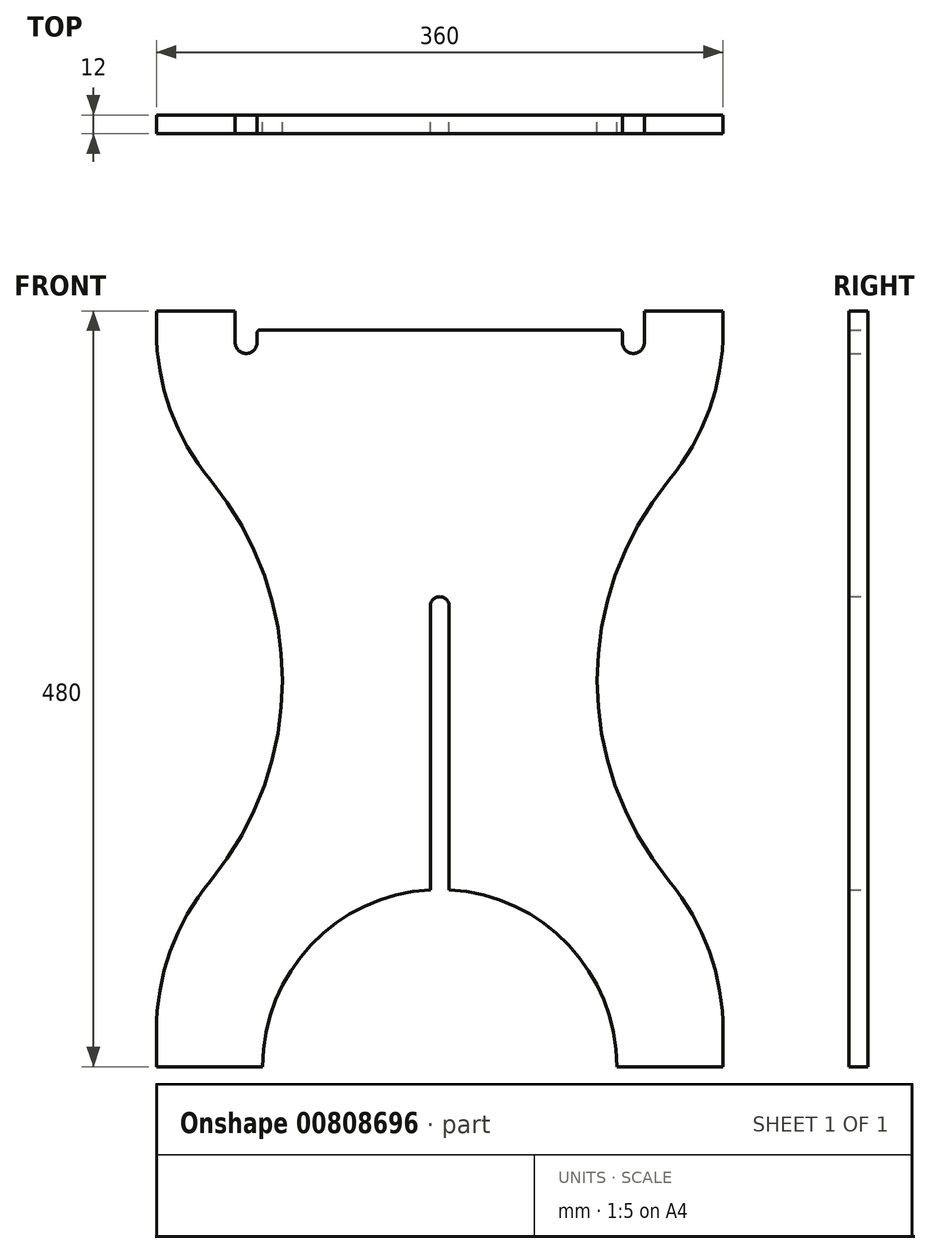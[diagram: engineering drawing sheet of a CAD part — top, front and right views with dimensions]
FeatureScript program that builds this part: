
annotation { "Feature Type Name" : "Feature", "Feature Type Description" : "" }
export const myFeature = defineFeature(function(context is Context, id is Id, definition is map)
    precondition{}
    {
        {
            var Q0;
            Q0=qCreatedBy(makeId("Front.planeOp"),FACE);
            var sketch = newSketch(context, id + "F0", { "sketchPlane" : qUnion([Q0])});
            skLineSegment(sketch, "E0.bottom", {"start": v(-180, -240) * mm, "end": v(-112.5, -240) * mm});
            skLineSegment(sketch, "E0.top", {"start": v(-180, 240) * mm, "end": v(-130, 240) * mm});
            skLineSegment(sketch, "E0.left", {"start": v(-180, -240) * mm, "end": v(-180, -217.42) * mm});
            skLineSegment(sketch, "E0.right", {"start": v(180, -240) * mm, "end": v(180, -217.42) * mm});
            skPoint(sketch, "E0.middle", {"position": v(0, 0) * mm});
            skLineSegment(sketch, "E1.0", {"start": v(-130, 228) * mm, "end": v(-130, 240) * mm});
            skLineSegment(sketch, "E2.0", {"start": v(130, 228) * mm, "end": v(130, 240) * mm});
            skLineSegment(sketch, "E3.trimOffspring", {"start": v(130, 240) * mm, "end": v(180, 240) * mm});
            skArc(sketch, "E4", {"start": v(112.5, -240) * mm, "mid": v(81.64, -162.6) * mm, "end": v(6, -127.66) * mm});
            skLineSegment(sketch, "E5.trimOffspring", {"start": v(112.5, -240) * mm, "end": v(180, -240) * mm});
            skArc(sketch, "E6", {"start": v(145.71, 132.55) * mm, "mid": v(100, 5.29) * mm, "end": v(145.71, -121.97) * mm});
            skArc(sketch, "E7", {"start": v(-145.71, -121.97) * mm, "mid": v(-100, 5.29) * mm, "end": v(-145.71, 132.55) * mm});
            skLineSegment(sketch, "E8.trimOffspring", {"start": v(-180, 228) * mm, "end": v(-180, 240) * mm});
            skLineSegment(sketch, "E9.trimOffspring", {"start": v(180, 228) * mm, "end": v(180, 240) * mm});
            skPoint(sketch, "E10.visualSharp", {"position": v(-180, 165.29) * mm});
            skArc(sketch, "E10.filletArc", {"start": v(-180, 228) * mm, "mid": v(-171.17, 177.3) * mm, "end": v(-145.71, 132.55) * mm});
            skPoint(sketch, "E11.visualSharp", {"position": v(-180, -154.71) * mm});
            skArc(sketch, "E11.filletArc", {"start": v(-145.71, -121.97) * mm, "mid": v(-171.17, -166.71) * mm, "end": v(-180, -217.42) * mm});
            skPoint(sketch, "E12.visualSharp", {"position": v(180, 165.29) * mm});
            skArc(sketch, "E12.filletArc", {"start": v(145.71, 132.55) * mm, "mid": v(171.17, 177.3) * mm, "end": v(180, 228) * mm});
            skPoint(sketch, "E13.visualSharp", {"position": v(180, -154.71) * mm});
            skArc(sketch, "E13.filletArc", {"start": v(180, -217.42) * mm, "mid": v(171.17, -166.71) * mm, "end": v(145.71, -121.97) * mm});
            skArc(sketch, "E14", {"start": v(116, 220) * mm, "mid": v(123, 213) * mm, "end": v(130, 220) * mm});
            skArc(sketch, "E15", {"start": v(-130, 220) * mm, "mid": v(-123, 213) * mm, "end": v(-116, 220) * mm});
            skLineSegment(sketch, "E16", {"start": v(-130, 228) * mm, "end": v(-130, 220) * mm});
            skLineSegment(sketch, "E17", {"start": v(-116, 220) * mm, "end": v(-116, 226) * mm});
            skLineSegment(sketch, "E18.trimOffspring", {"start": v(-114, 228) * mm, "end": v(114, 228) * mm});
            skLineSegment(sketch, "E19", {"start": v(130, 228) * mm, "end": v(130, 220) * mm});
            skLineSegment(sketch, "E20", {"start": v(116, 220) * mm, "end": v(116, 226) * mm});
            skPoint(sketch, "E21.visualSharp", {"position": v(-115.99, 228) * mm});
            skArc(sketch, "E21.filletArc", {"start": v(-114, 228) * mm, "mid": v(-115.4, 227.42) * mm, "end": v(-116, 226) * mm});
            skPoint(sketch, "E22.visualSharp", {"position": v(116, 228) * mm});
            skArc(sketch, "E22.filletArc", {"start": v(116, 226) * mm, "mid": v(115.41, 227.41) * mm, "end": v(114, 228) * mm});
            skLineSegment(sketch, "E23.0", {"start": v(6, -127.66) * mm, "end": v(6, 52.5) * mm});
            skLineSegment(sketch, "E24.0", {"start": v(-6, -127.66) * mm, "end": v(-6, 52.5) * mm});
            skArc(sketch, "E25", {"start": v(6, 52.5) * mm, "mid": v(0, 58.5) * mm, "end": v(-6, 52.5) * mm});
            skArc(sketch, "E26.trimOffspring", {"start": v(-6, -127.66) * mm, "mid": v(-81.64, -162.6) * mm, "end": v(-112.5, -240) * mm});
            skSolve(sketch);
        }
        {
            var Q0;
            Q0=makeQuery(id+"F0.imprint","IMPRINT",FACE,{"disambiguationData":[TD([[makeQuery(id+"F0.imprint","IMPRINT",EDGE,{"derivedFrom":sQuery(id+"F0.wireOp",EDGE,"E0.bottom")}),1.0]])]});
            extrude(context, id + "F1", {"entities" : qUnion([Q0]), "depth" : 12 * mm, "offsetDistance" : 25 * mm});
        }
    });
